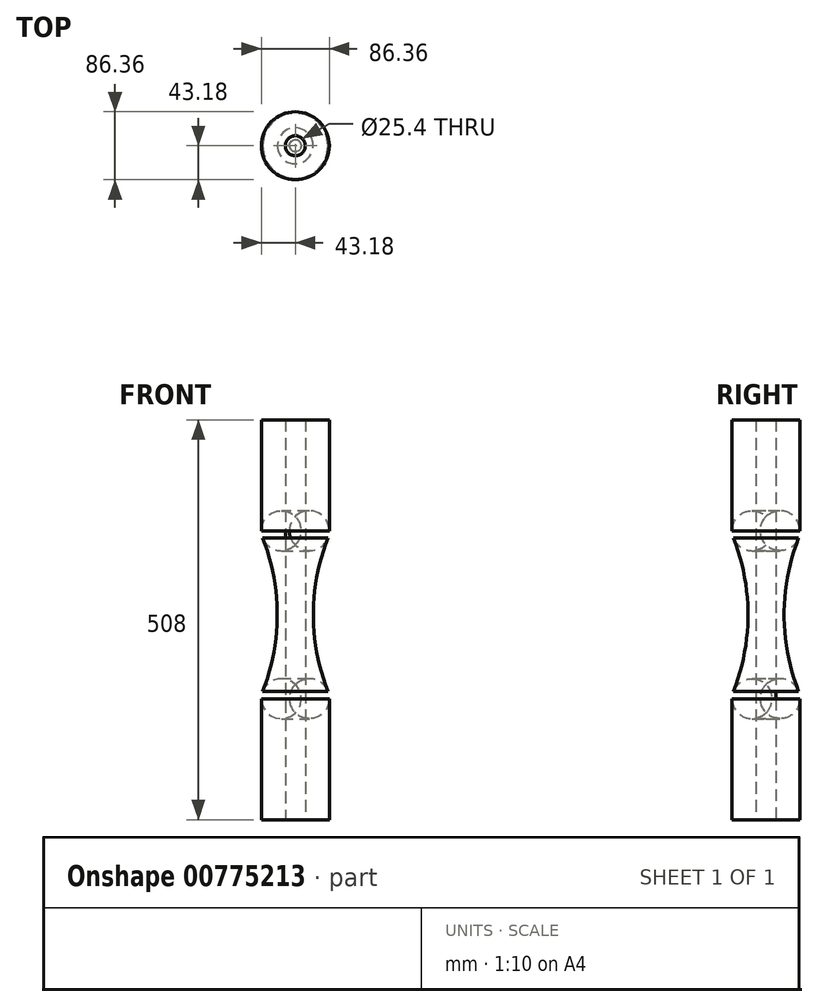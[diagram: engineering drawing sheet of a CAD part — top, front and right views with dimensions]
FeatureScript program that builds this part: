
annotation { "Feature Type Name" : "Feature", "Feature Type Description" : "" }
export const myFeature = defineFeature(function(context is Context, id is Id, definition is map)
    precondition{}
    {
        {
            var Q0;
            Q0=qCreatedBy(makeId("Top.planeOp"),FACE);
            var sketch = newSketch(context, id + "F0", { "sketchPlane" : qUnion([Q0])});
            skCircle(sketch, "E0", {"center": v(0, 0) * mm, "radius": 43.18 * mm});
            skSolve(sketch);
        }
        {
            var Q0;
            Q0 = qSketchRegion(id + "F0", true);
            extrude(context, id + "F1", {"entities" : qUnion([Q0]), "depth" : 508 * mm, "offsetDistance" : 25.4 * mm});
        }
        {
            var Q0;
            Q0=qCreatedBy(makeId("Front.planeOp"),FACE);
            var sketch = newSketch(context, id + "F2", { "sketchPlane" : qUnion([Q0])});
            skArc(sketch, "E1", {"start": v(-98.22, 75.27) * mm, "mid": v(-22.93, 256.9) * mm, "end": v(-93.25, 440.5) * mm});
            skLineSegment(sketch, "E2", {"start": v(-93.25, 440.5) * mm, "end": v(-384.33, 258.43) * mm});
            skLineSegment(sketch, "E3", {"start": v(-384.33, 258.43) * mm, "end": v(-98.22, 75.27) * mm});
            skSolve(sketch);
        }
        {
            var Q0;
            Q0=makeQuery(id+"F2.imprint","IMPRINT",FACE,{"disambiguationData":[TD([[makeQuery(id+"F2.imprint","IMPRINT",EDGE,{"derivedFrom":sQuery(id+"F2.wireOp",EDGE,"E1")}),1.0]])]});
            var Q1;
            Q1=makeQuery(id+"F1.opExtrude","SWEPT_FACE",FACE,{"disambiguationData":[OSD([sQuery(id+"F0.wireOp",EDGE,"E0")])]});
            revolve(context, id + "F3", {"operationType" : NewBodyOperationType.REMOVE, "surfaceOperationType" : NewSurfaceOperationType.NEW, "entities" : qUnion([Q0]), "axis" : qUnion([Q1]), "revolveType" : RevolveType.FULL, "oppositeDirection" : true});
        }
        {
            var Q0;
            Q0=makeQuery(id+"F3.boolean.opBoolean","INTERSECT",EDGE,{"disambiguationData":[OD(1.0)],"derivedFrom":[makeQuery(id+"F1.opExtrude","SWEPT_FACE",FACE,{"disambiguationData":[OSD([sQuery(id+"F0.wireOp",EDGE,"E0")])]}),makeQuery(id+"F3.opRevolve","SWEPT_FACE",FACE,{"disambiguationData":[OSD([sQuery(id+"F2.wireOp",EDGE,"E1")])]})]});
            var Q1;
            Q1=makeQuery(id+"F3.boolean.opBoolean","INTERSECT",EDGE,{"disambiguationData":[OD(0.0)],"derivedFrom":[makeQuery(id+"F1.opExtrude","SWEPT_FACE",FACE,{"disambiguationData":[OSD([sQuery(id+"F0.wireOp",EDGE,"E0")])]}),makeQuery(id+"F3.opRevolve","SWEPT_FACE",FACE,{"disambiguationData":[OSD([sQuery(id+"F2.wireOp",EDGE,"E1")])]})]});
            fillet(context, id + "F4", {"entities" : qUnion([Q0, Q1]), "radius" : 25.4 * mm, "tangentPropagation" : true, "allowEdgeOverflow" : false});
        }
        {
            var Q0;
            Q0=makeQuery(id+"F1.opExtrude","CAP_FACE",FACE,{"disambiguationData":[OSD([sQuery(id+"F0.wireOp",EDGE,"E0")])],"isStart":true});
            var sketch = newSketch(context, id + "F5", { "sketchPlane" : qUnion([Q0])});
            skCircle(sketch, "E4", {"center": v(0, 0) * mm, "radius": 12.7 * mm});
            skSolve(sketch);
        }
        {
            var Q0;
            Q0=makeQuery(id+"F5.imprint","IMPRINT",FACE,{"disambiguationData":[TD([[makeQuery(id+"F5.imprint","IMPRINT",EDGE,{"derivedFrom":sQuery(id+"F5.wireOp",EDGE,"E4")}),1.0]])]});
            extrude(context, id + "F6", {"entities" : qUnion([Q0]), "operationType" : NewBodyOperationType.REMOVE, "endBound" : BoundingType.THROUGH_ALL, "oppositeDirection" : true, "depth" : 25.4 * mm, "offsetDistance" : 25.4 * mm});
        }
    });
